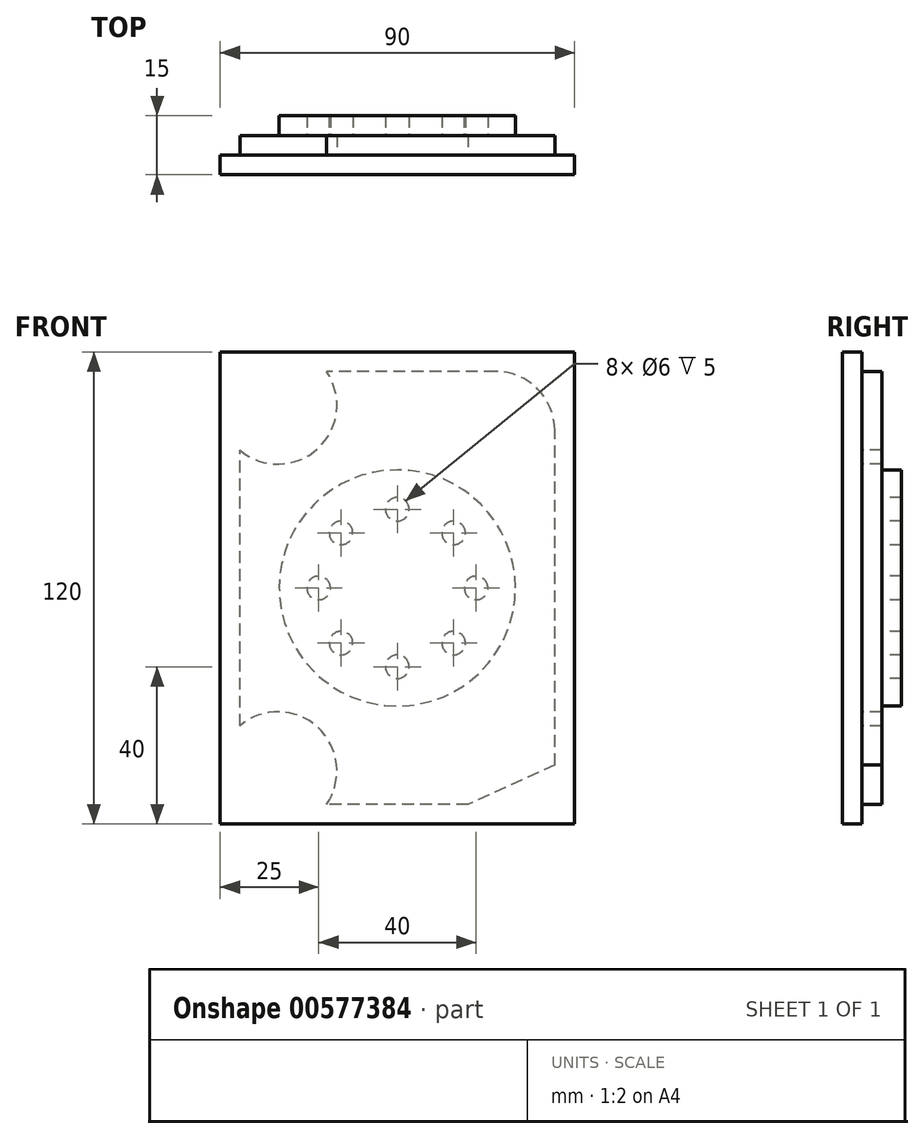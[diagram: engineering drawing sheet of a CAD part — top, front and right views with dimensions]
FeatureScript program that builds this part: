
annotation { "Feature Type Name" : "Feature", "Feature Type Description" : "" }
export const myFeature = defineFeature(function(context is Context, id is Id, definition is map)
    precondition{}
    {
        {
            var Q0;
            Q0=qCreatedBy(makeId("Front.planeOp"),FACE);
            var sketch = newSketch(context, id + "F0", { "sketchPlane" : qUnion([Q0])});
            skLineSegment(sketch, "E0", {"start": v(0, 0) * mm, "end": v(0, 120) * mm});
            skLineSegment(sketch, "E1", {"start": v(0, 120) * mm, "end": v(90, 120) * mm});
            skLineSegment(sketch, "E2", {"start": v(90, 120) * mm, "end": v(90, 0) * mm});
            skLineSegment(sketch, "E3", {"start": v(0, 0) * mm, "end": v(90, 0) * mm});
            skSolve(sketch);
        }
        {
            var Q0;
            Q0=makeQuery(id+"F0.imprint","IMPRINT",FACE,{"disambiguationData":[TD([[makeQuery(id+"F0.imprint","IMPRINT",EDGE,{"derivedFrom":sQuery(id+"F0.wireOp",EDGE,"E0")}),-1.0]])]});
            extrude(context, id + "F1", {"entities" : qUnion([Q0]), "depth" : 5 * mm, "offsetDistance" : 25 * mm});
        }
        {
            var Q0;
            Q0=makeQuery(id+"F1.opExtrude","CAP_FACE",FACE,{"disambiguationData":[OSD([sQuery(id+"F0.wireOp",EDGE,"E0"),sQuery(id+"F0.wireOp",EDGE,"E1"),sQuery(id+"F0.wireOp",EDGE,"E2"),sQuery(id+"F0.wireOp",EDGE,"E3")])],"isStart":true});
            var sketch = newSketch(context, id + "F2", { "sketchPlane" : qUnion([Q0])});
            skLineSegment(sketch, "E4", {"start": v(-63, 5) * mm, "end": v(-27, 5) * mm});
            skLineSegment(sketch, "E5", {"start": v(-5, 25) * mm, "end": v(-5, 95) * mm});
            skLineSegment(sketch, "E6", {"start": v(-85, 15) * mm, "end": v(-85, 100) * mm});
            skLineSegment(sketch, "E7", {"start": v(-70, 115) * mm, "end": v(-27, 115) * mm});
            skArc(sketch, "E8", {"start": v(-27, 115) * mm, "mid": v(-24.74, 95.38) * mm, "end": v(-5, 95) * mm});
            skLineSegment(sketch, "E9", {"start": v(-85, 15) * mm, "end": v(-63, 5) * mm});
            skArc(sketch, "E10", {"start": v(-5, 25) * mm, "mid": v(-24.74, 24.62) * mm, "end": v(-27, 5) * mm});
            skPoint(sketch, "E11.visualSharp", {"position": v(-85, 115) * mm});
            skArc(sketch, "E11.filletArc", {"start": v(-70, 115) * mm, "mid": v(-80.6, 110.6) * mm, "end": v(-85, 100) * mm});
            skSolve(sketch);
        }
        {
            var Q0;
            Q0=makeQuery(id+"F2.imprint","IMPRINT",FACE,{"disambiguationData":[TD([[makeQuery(id+"F2.imprint","IMPRINT",EDGE,{"derivedFrom":sQuery(id+"F2.wireOp",EDGE,"E4")}),1.0]])]});
            extrude(context, id + "F3", {"entities" : qUnion([Q0]), "operationType" : NewBodyOperationType.ADD, "depth" : 5 * mm, "offsetDistance" : 25 * mm});
        }
        {
            var Q0;
            Q0=makeQuery(id+"F3.opExtrude","CAP_FACE",FACE,{"disambiguationData":[OSD([sQuery(id+"F2.wireOp",EDGE,"E4"),sQuery(id+"F2.wireOp",EDGE,"E5"),sQuery(id+"F2.wireOp",EDGE,"E6"),sQuery(id+"F2.wireOp",EDGE,"E7"),sQuery(id+"F2.wireOp",EDGE,"E8"),sQuery(id+"F2.wireOp",EDGE,"E9"),sQuery(id+"F2.wireOp",EDGE,"E10"),sQuery(id+"F2.wireOp",EDGE,"E11.filletArc")])],"isStart":false});
            var sketch = newSketch(context, id + "F4", { "sketchPlane" : qUnion([Q0])});
            skCircle(sketch, "E12", {"center": v(-45, 60) * mm, "radius": 30 * mm});
            skCircle(sketch, "E13", {"center": v(-45, 60) * mm, "radius": 20 * mm, "construction": true});
            skCircle(sketch, "E14", {"center": v(-45, 40) * mm, "radius": 3 * mm});
            skCircle(sketch, "E15", {"center": v(-45, 80) * mm, "radius": 3 * mm});
            skCircle(sketch, "E16", {"center": v(-25, 60) * mm, "radius": 3 * mm});
            skCircle(sketch, "E17", {"center": v(-65, 60) * mm, "radius": 3 * mm});
            skCircle(sketch, "E18", {"center": v(-59.3, 46.02) * mm, "radius": 3 * mm});
            skCircle(sketch, "E19", {"center": v(-30.7, 46.02) * mm, "radius": 3 * mm});
            skCircle(sketch, "E20", {"center": v(-30.7, 73.98) * mm, "radius": 3 * mm});
            skCircle(sketch, "E21", {"center": v(-59.3, 73.98) * mm, "radius": 3 * mm});
            skSolve(sketch);
        }
        {
            var Q0;
            Q0=makeQuery(id+"F4.imprint","IMPRINT",FACE,{"disambiguationData":[TD([[makeQuery(id+"F4.imprint","IMPRINT",EDGE,{"derivedFrom":sQuery(id+"F4.wireOp",EDGE,"E12")}),1.0]])]});
            extrude(context, id + "F5", {"entities" : qUnion([Q0]), "operationType" : NewBodyOperationType.ADD, "depth" : 5 * mm, "offsetDistance" : 25 * mm});
        }
    });
